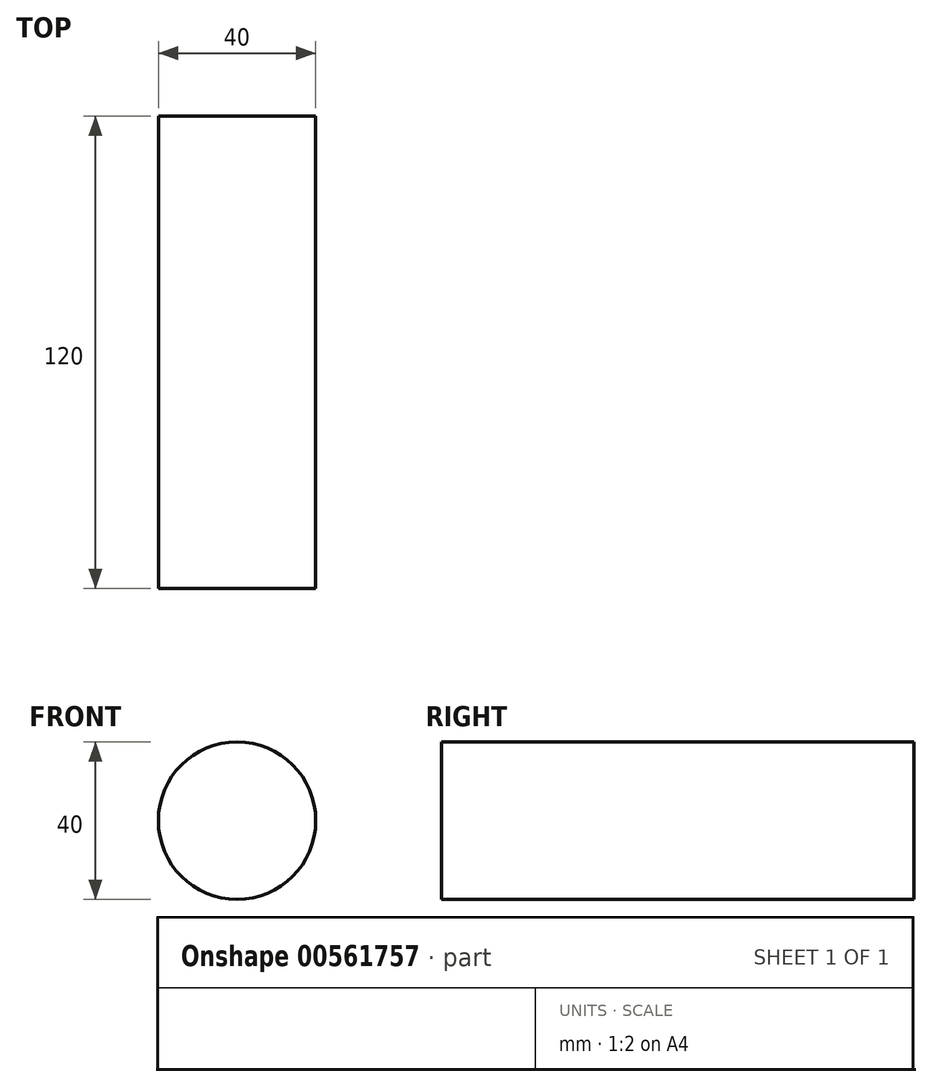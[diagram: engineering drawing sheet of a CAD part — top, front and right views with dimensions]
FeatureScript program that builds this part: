
annotation { "Feature Type Name" : "Feature", "Feature Type Description" : "" }
export const myFeature = defineFeature(function(context is Context, id is Id, definition is map)
    precondition{}
    {
        {
            var Q0;
            Q0=qCreatedBy(makeId("Front.planeOp"),FACE);
            var sketch = newSketch(context, id + "F0", { "sketchPlane" : qUnion([Q0])});
            skCircle(sketch, "E0", {"center": v(0, 0) * mm, "radius": 20 * mm});
            skSolve(sketch);
        }
        {
            var Q0;
            Q0=qCreatedBy(makeId("Right.planeOp"),FACE);
            var sketch = newSketch(context, id + "F1", { "sketchPlane" : qUnion([Q0])});
            skLineSegment(sketch, "E1", {"start": v(0, 0) * mm, "end": v(120, 0) * mm});
            skSolve(sketch);
        }
        {
            var Q0;
            Q0=makeQuery(id+"F0.imprint","IMPRINT",FACE,{"disambiguationData":[TD([[makeQuery(id+"F0.imprint","IMPRINT",EDGE,{"derivedFrom":sQuery(id+"F0.wireOp",EDGE,"E0")}),1.0]])]});
            var Q1;
            Q1=sQuery(id+"F1.wireOp",EDGE,"E1");
            sweep(context, id + "F2", {"profiles" : qUnion([Q0]), "path" : qUnion([Q1])});
        }
    });
